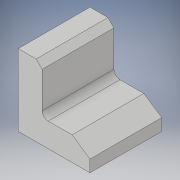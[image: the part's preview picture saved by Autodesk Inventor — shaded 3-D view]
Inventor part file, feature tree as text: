
AUTODESK INVENTOR PART (.ipt)
format: ipt  version: 2017 (Build 210142000, 142)  size: 105,984 bytes
history: native  units: in
note: dims shown in document units (in); Inventor stores cm internally (conversion verified against a paired STEP export)
features: chamfer x2, extrude x1, fillet x1, sketch x1
ambient origin geometry x8: Origin, YZ Plane, XZ Plane, XY Plane, X Axis, Y Axis, Z Axis, Center Point
bodies: Solid1 (feature_tree)
feature tree (5):
  extrude  "Extrusion1"  Depth=0.5in
  fillet  "Fillet3"  Radius=1.0in
  chamfer  "Chamfer1"  Distance=1.0in
  chamfer  "Chamfer2"  Distance=1.5in
  sketch  "Sketch1"  dims[d0=1.5in d1=0.5in d2=1.0in d3=1.0in d4=1.5in d5=0.0in d8=0.125in d9=0.125in d10=0.125in d11=45.0deg d12=0.25in d13=0.375in d14=45.0deg]
